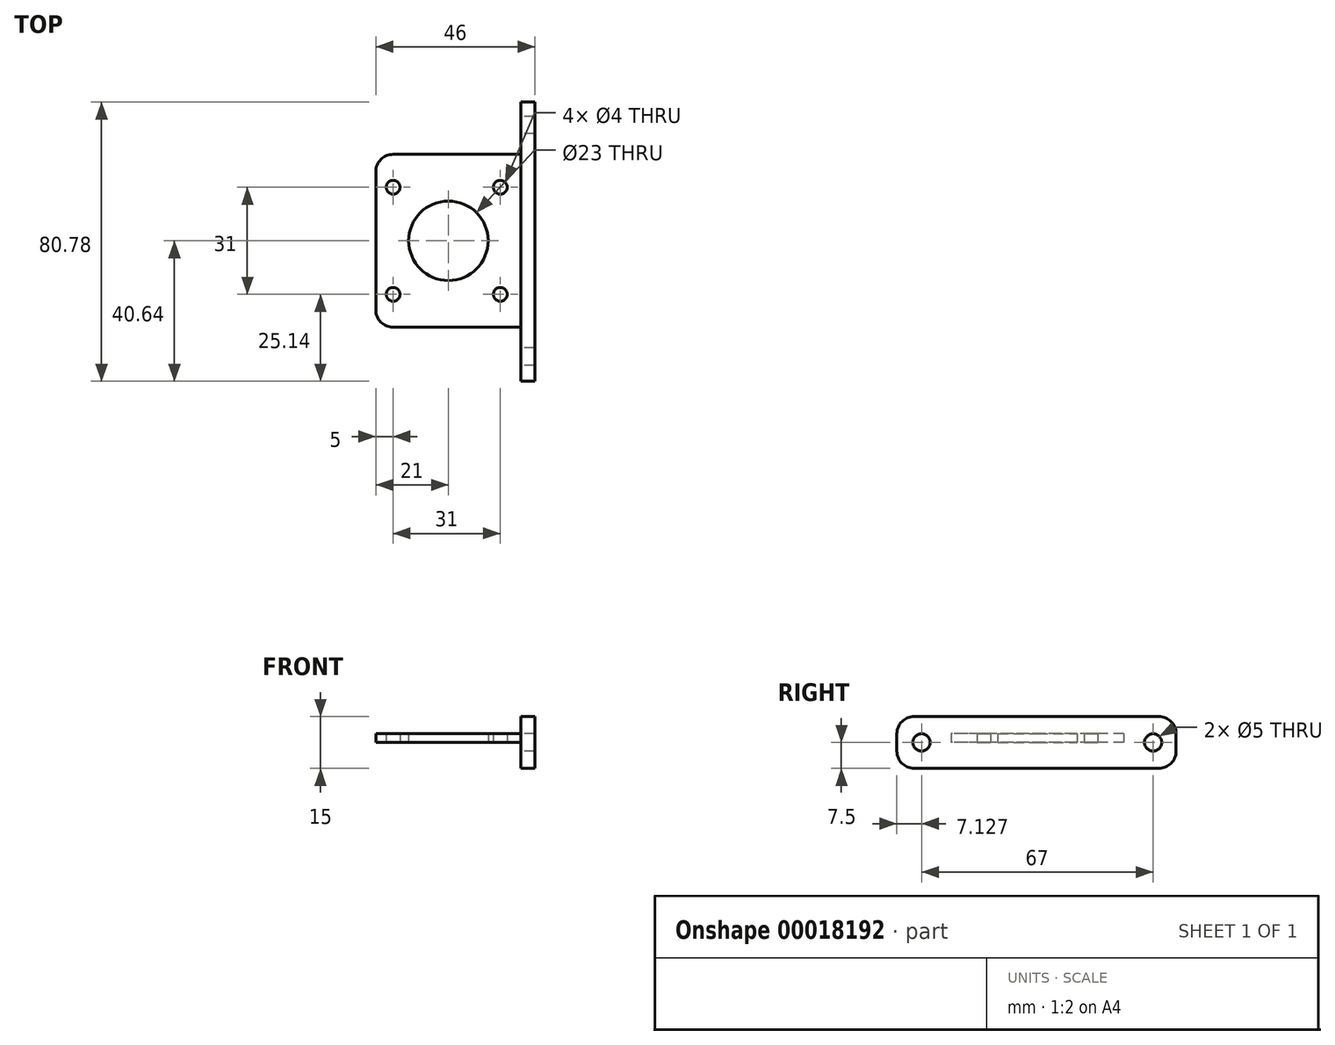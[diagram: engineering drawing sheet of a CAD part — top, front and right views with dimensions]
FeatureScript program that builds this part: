
annotation { "Feature Type Name" : "Feature", "Feature Type Description" : "" }
export const myFeature = defineFeature(function(context is Context, id is Id, definition is map)
    precondition{}
    {
        {
            var Q0;
            Q0=qCreatedBy(makeId("Top.planeOp"),FACE);
            var sketch = newSketch(context, id + "F0", { "sketchPlane" : qUnion([Q0])});
            skLineSegment(sketch, "E0.rect.bottom", {"start": v(-21, 25) * mm, "end": v(21, 25) * mm});
            skLineSegment(sketch, "E0.rect.top", {"start": v(-21, -25) * mm, "end": v(21, -25) * mm});
            skLineSegment(sketch, "E0.rect.left", {"start": v(-21, 25) * mm, "end": v(-21, -25) * mm});
            skLineSegment(sketch, "E0.rect.right", {"start": v(21, 25) * mm, "end": v(21, -25) * mm});
            skPoint(sketch, "E0.rect.middle", {"position": v(0, 0) * mm});
            skLineSegment(sketch, "E1", {"start": v(-21, 15.5) * mm, "end": v(21, 15.5) * mm, "construction": true});
            skLineSegment(sketch, "E2", {"start": v(21, -15.5) * mm, "end": v(-21, -15.5) * mm, "construction": true});
            skLineSegment(sketch, "E3", {"start": v(-16, -25) * mm, "end": v(-16, 25) * mm, "construction": true});
            skLineSegment(sketch, "E4", {"start": v(15, -25) * mm, "end": v(15, 25) * mm, "construction": true});
            skCircle(sketch, "E5", {"center": v(-16, 15.5) * mm, "radius": 2 * mm});
            skCircle(sketch, "E6", {"center": v(15, 15.5) * mm, "radius": 2 * mm});
            skCircle(sketch, "E7", {"center": v(-16, -15.5) * mm, "radius": 2 * mm});
            skCircle(sketch, "E8", {"center": v(15, -15.5) * mm, "radius": 2 * mm});
            skLineSegment(sketch, "E9", {"start": v(-21, 0) * mm, "end": v(21, 0) * mm, "construction": true});
            skCircle(sketch, "E10", {"center": v(0, 0) * mm, "radius": 11.5 * mm});
            skSolve(sketch);
        }
        {
            var Q0;
            Q0=qSketchRegion(id+"F0",true);
            var Q1;
            Q1=makeQuery(id+"F0.imprint","IMPRINT",FACE,{"disambiguationData":[TD([[makeQuery(id+"F0.imprint","IMPRINT",EDGE,{"derivedFrom":sQuery(id+"F0.wireOp",EDGE,"E0.rect.bottom")}),-1.0]])]});
            extrude(context, id + "F1", {"entities" : qUnion([Q0, Q1]), "depth" : 2.5 * mm});
        }
        {
            var Q0;
            Q0=makeQuery(id+"F1.opExtrude","SWEPT_FACE",FACE,{"disambiguationData":[OSD([sQuery(id+"F0.wireOp",EDGE,"E0.rect.right")])]});
            var sketch = newSketch(context, id + "F2", { "sketchPlane" : qUnion([Q0])});
            skLineSegment(sketch, "E11.bottom", {"start": v(-40.64, 7.5) * mm, "end": v(40.14, 7.5) * mm});
            skLineSegment(sketch, "E11.top", {"start": v(-40.64, -7.5) * mm, "end": v(40.14, -7.5) * mm});
            skLineSegment(sketch, "E11.left", {"start": v(-40.64, 7.5) * mm, "end": v(-40.64, -7.5) * mm});
            skLineSegment(sketch, "E11.right", {"start": v(40.14, 7.5) * mm, "end": v(40.14, -7.5) * mm});
            skLineSegment(sketch, "E12", {"start": v(-40.64, 0) * mm, "end": v(40.14, 0) * mm, "construction": true});
            skCircle(sketch, "E13", {"center": v(-33.51, 0) * mm, "radius": 2.5 * mm});
            skCircle(sketch, "E14", {"center": v(33.49, 0) * mm, "radius": 2.5 * mm});
            skSolve(sketch);
        }
        {
            var Q0;
            Q0=qSketchRegion(id+"F2",true);
            extrude(context, id + "F3", {"entities" : qUnion([Q0]), "operationType" : NewBodyOperationType.ADD, "depth" : 4 * mm});
        }
        {
            var Q0;
            Q0=makeQuery(id+"F3.opExtrude","SWEPT_EDGE",EDGE,{"disambiguationData":[OSD([sQuery(id+"F2.wireOp",EDGE,"E11.bottom"),sQuery(id+"F2.wireOp",EDGE,"E11.left")])]});
            var Q1;
            Q1=makeQuery(id+"F3.opExtrude","SWEPT_EDGE",EDGE,{"disambiguationData":[OSD([sQuery(id+"F2.wireOp",EDGE,"E11.top"),sQuery(id+"F2.wireOp",EDGE,"E11.left")])]});
            var Q2;
            Q2=makeQuery(id+"F3.opExtrude","SWEPT_EDGE",EDGE,{"disambiguationData":[OSD([sQuery(id+"F2.wireOp",EDGE,"E11.bottom"),sQuery(id+"F2.wireOp",EDGE,"E11.right")])]});
            var Q3;
            Q3=makeQuery(id+"F3.opExtrude","SWEPT_EDGE",EDGE,{"disambiguationData":[OSD([sQuery(id+"F2.wireOp",EDGE,"E11.top"),sQuery(id+"F2.wireOp",EDGE,"E11.right")])]});
            fillet(context, id + "F4", {"entities" : qUnion([Q0, Q1, Q2, Q3]), "radius" : 5 * mm, "tangentPropagation" : true, "allowEdgeOverflow" : false});
        }
        {
            var Q0;
            Q0=makeQuery(id+"F1.opExtrude","SWEPT_EDGE",EDGE,{"disambiguationData":[OSD([sQuery(id+"F0.wireOp",EDGE,"E0.rect.top"),sQuery(id+"F0.wireOp",EDGE,"E0.rect.left")])]});
            var Q1;
            Q1=makeQuery(id+"F1.opExtrude","SWEPT_EDGE",EDGE,{"disambiguationData":[OSD([sQuery(id+"F0.wireOp",EDGE,"E0.rect.bottom"),sQuery(id+"F0.wireOp",EDGE,"E0.rect.left")])]});
            fillet(context, id + "F5", {"entities" : qUnion([Q0, Q1]), "radius" : 5 * mm, "tangentPropagation" : true, "allowEdgeOverflow" : false});
        }
    });
